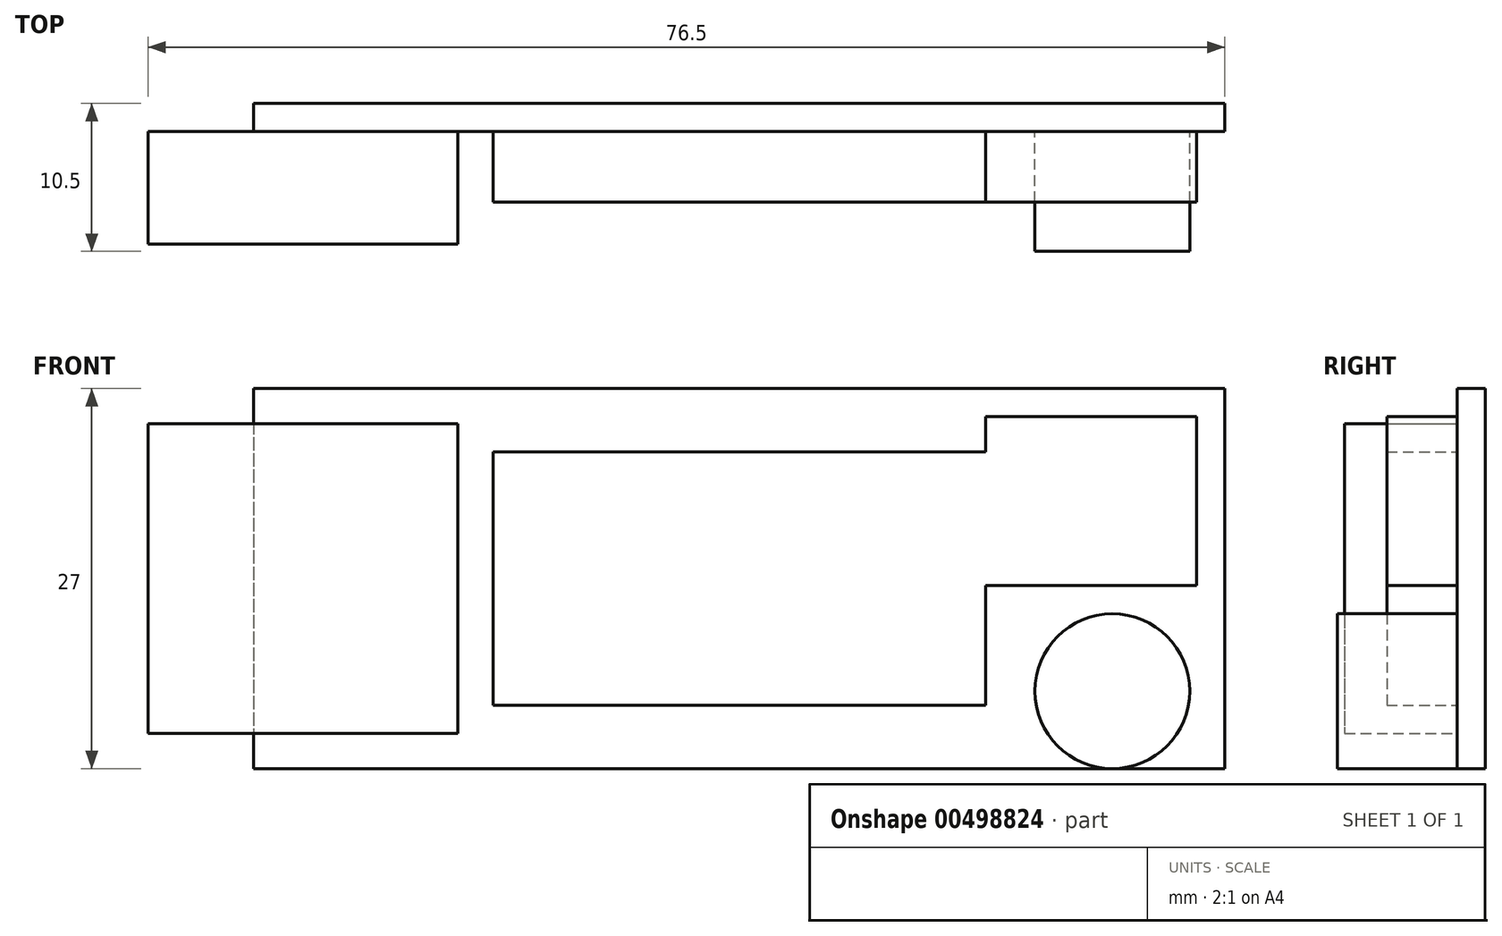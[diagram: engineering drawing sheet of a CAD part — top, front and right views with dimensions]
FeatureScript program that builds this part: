
annotation { "Feature Type Name" : "Feature", "Feature Type Description" : "" }
export const myFeature = defineFeature(function(context is Context, id is Id, definition is map)
    precondition{}
    {
        {
            var Q0;
            Q0=qCreatedBy(makeId("Front.planeOp"),FACE);
            var sketch = newSketch(context, id + "F0", { "sketchPlane" : qUnion([Q0])});
            skLineSegment(sketch, "E0.bottom", {"start": v(-34.5, 13.5) * mm, "end": v(34.5, 13.5) * mm});
            skLineSegment(sketch, "E0.top", {"start": v(-34.5, -13.5) * mm, "end": v(34.5, -13.5) * mm});
            skLineSegment(sketch, "E0.left", {"start": v(-34.5, 13.5) * mm, "end": v(-34.5, -13.5) * mm});
            skLineSegment(sketch, "E0.right", {"start": v(34.5, 13.5) * mm, "end": v(34.5, -13.5) * mm});
            skLineSegment(sketch, "E1", {"start": v(34.5, 13.5) * mm, "end": v(-34.5, -13.5) * mm, "construction": true});
            skLineSegment(sketch, "E2", {"start": v(-34.5, 13.5) * mm, "end": v(34.5, -13.5) * mm, "construction": true});
            skSolve(sketch);
        }
        {
            var Q0;
            Q0 = qSketchRegion(id + "F0", true);
            extrude(context, id + "F1", {"entities" : qUnion([Q0]), "depth" : 2 * mm});
        }
        {
            var Q0;
            Q0=makeQuery(id+"F1.opExtrude","CAP_FACE",FACE,{"disambiguationData":[OSD([sQuery(id+"F0.wireOp",EDGE,"E0.bottom"),sQuery(id+"F0.wireOp",EDGE,"E0.top"),sQuery(id+"F0.wireOp",EDGE,"E0.left"),sQuery(id+"F0.wireOp",EDGE,"E0.right")])],"isStart":false});
            var sketch = newSketch(context, id + "F2", { "sketchPlane" : qUnion([Q0])});
            skLineSegment(sketch, "E3.bottom", {"start": v(-42, 11) * mm, "end": v(-20, 11) * mm});
            skLineSegment(sketch, "E3.top", {"start": v(-42, -11) * mm, "end": v(-20, -11) * mm});
            skLineSegment(sketch, "E3.left", {"start": v(-42, 11) * mm, "end": v(-42, -11) * mm});
            skLineSegment(sketch, "E3.right", {"start": v(-20, 11) * mm, "end": v(-20, -11) * mm});
            skSolve(sketch);
        }
        {
            var Q0;
            Q0 = qSketchRegion(id + "F2", true);
            extrude(context, id + "F3", {"entities" : qUnion([Q0]), "operationType" : NewBodyOperationType.ADD, "depth" : 8 * mm});
        }
        {
            var Q0;
            Q0=makeQuery(id+"F1.opExtrude","CAP_FACE",FACE,{"disambiguationData":[OSD([sQuery(id+"F0.wireOp",EDGE,"E0.bottom"),sQuery(id+"F0.wireOp",EDGE,"E0.top"),sQuery(id+"F0.wireOp",EDGE,"E0.left"),sQuery(id+"F0.wireOp",EDGE,"E0.right")])],"isStart":false});
            var sketch = newSketch(context, id + "F4", { "sketchPlane" : qUnion([Q0])});
            skLineSegment(sketch, "E4.bottom", {"start": v(-17.5, 9) * mm, "end": v(17.5, 9) * mm});
            skLineSegment(sketch, "E4.top", {"start": v(-17.5, -9) * mm, "end": v(17.5, -9) * mm});
            skLineSegment(sketch, "E4.left", {"start": v(-17.5, 9) * mm, "end": v(-17.5, -9) * mm});
            skLineSegment(sketch, "E4.right", {"start": v(17.5, 9) * mm, "end": v(17.5, -9) * mm});
            skSolve(sketch);
        }
        {
            var Q0;
            Q0 = qSketchRegion(id + "F4", true);
            extrude(context, id + "F5", {"entities" : qUnion([Q0]), "operationType" : NewBodyOperationType.ADD, "depth" : 5 * mm});
        }
        {
            var Q0;
            Q0=makeQuery(id+"F1.opExtrude","CAP_FACE",FACE,{"disambiguationData":[OSD([sQuery(id+"F0.wireOp",EDGE,"E0.bottom"),sQuery(id+"F0.wireOp",EDGE,"E0.top"),sQuery(id+"F0.wireOp",EDGE,"E0.left"),sQuery(id+"F0.wireOp",EDGE,"E0.right")])],"isStart":false});
            var sketch = newSketch(context, id + "F6", { "sketchPlane" : qUnion([Q0])});
            skLineSegment(sketch, "E5.bottom", {"start": v(17.5, 11.5) * mm, "end": v(32.5, 11.5) * mm});
            skLineSegment(sketch, "E5.top", {"start": v(17.5, -0.5) * mm, "end": v(32.5, -0.5) * mm});
            skLineSegment(sketch, "E5.left", {"start": v(17.5, 11.5) * mm, "end": v(17.5, -0.5) * mm});
            skLineSegment(sketch, "E5.right", {"start": v(32.5, 11.5) * mm, "end": v(32.5, -0.5) * mm});
            skSolve(sketch);
        }
        {
            var Q0;
            Q0 = qSketchRegion(id + "F6", true);
            extrude(context, id + "F7", {"entities" : qUnion([Q0]), "operationType" : NewBodyOperationType.ADD, "depth" : 5 * mm});
        }
        {
            var Q0;
            Q0=makeQuery(id+"F1.opExtrude","CAP_FACE",FACE,{"disambiguationData":[OSD([sQuery(id+"F0.wireOp",EDGE,"E0.bottom"),sQuery(id+"F0.wireOp",EDGE,"E0.top"),sQuery(id+"F0.wireOp",EDGE,"E0.left"),sQuery(id+"F0.wireOp",EDGE,"E0.right")])],"isStart":false});
            var sketch = newSketch(context, id + "F8", { "sketchPlane" : qUnion([Q0])});
            skCircle(sketch, "E6", {"center": v(26.5, -8) * mm, "radius": 5.5 * mm});
            skSolve(sketch);
        }
        {
            var Q0;
            Q0 = qSketchRegion(id + "F8", true);
            extrude(context, id + "F9", {"entities" : qUnion([Q0]), "operationType" : NewBodyOperationType.ADD, "depth" : 8.5 * mm});
        }
    });
